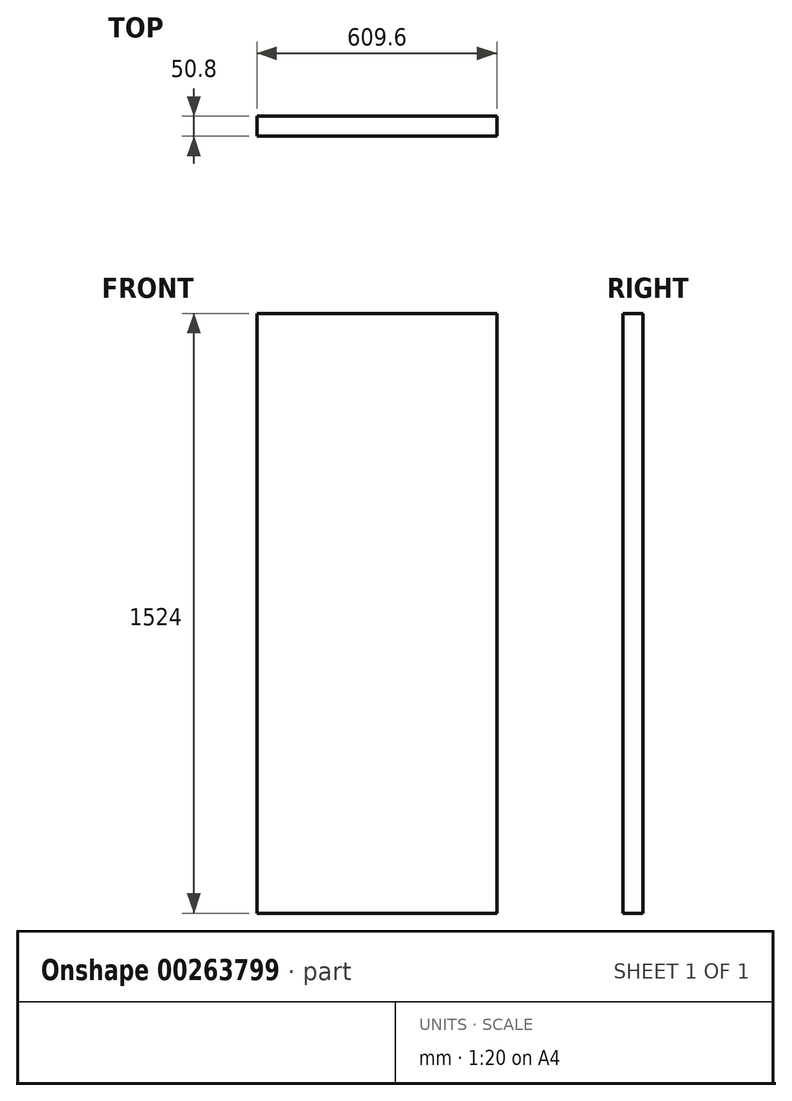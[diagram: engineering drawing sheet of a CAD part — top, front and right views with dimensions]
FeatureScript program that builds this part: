
annotation { "Feature Type Name" : "Feature", "Feature Type Description" : "" }
export const myFeature = defineFeature(function(context is Context, id is Id, definition is map)
    precondition{}
    {
        {
            var Q0;
            Q0=qCreatedBy(makeId("Front.planeOp"),FACE);
            var sketch = newSketch(context, id + "F0", { "sketchPlane" : qUnion([Q0])});
            skLineSegment(sketch, "E0.bottom", {"start": v(-1076.22, -213.97) * mm, "end": v(-466.62, -213.97) * mm});
            skLineSegment(sketch, "E0.top", {"start": v(-1076.22, -1737.97) * mm, "end": v(-466.62, -1737.97) * mm});
            skLineSegment(sketch, "E0.left", {"start": v(-1076.22, -213.97) * mm, "end": v(-1076.22, -1737.97) * mm});
            skLineSegment(sketch, "E0.right", {"start": v(-466.62, -213.97) * mm, "end": v(-466.62, -1737.97) * mm});
            skSolve(sketch);
        }
        {
            var Q0;
            Q0 = qSketchRegion(id + "F0", true);
            extrude(context, id + "F1", {"entities" : qUnion([Q0]), "depth" : 50.8 * mm});
        }
    });
